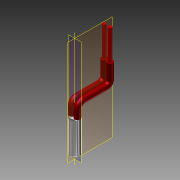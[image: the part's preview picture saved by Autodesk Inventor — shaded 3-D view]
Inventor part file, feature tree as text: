
AUTODESK INVENTOR PART (.ipt)
format: ipt  version: 2015 (Build 190159000, 159)  size: 135,680 bytes
history: native  units: mm
features: extrude x2, chamfer x1, sweep x1, other x1, projected_geometry x1
ambient origin geometry x8: Origin, YZ Plane, XZ Plane, XY Plane, X Axis, Y Axis, Z Axis, Center Point
bodies: Solid1 (feature_tree)
feature tree (6):
  extrude  "Extrusión1"  Depth=6.0mm
  chamfer  "Chaflán1"  Distance=20.0mm
  sweep  "Barrido1"
  extrude  "Extrusión2"  Depth=20.0mm
  other  "Eje de trabajo1"
  projected_geometry  "Contorno proyectado1"
